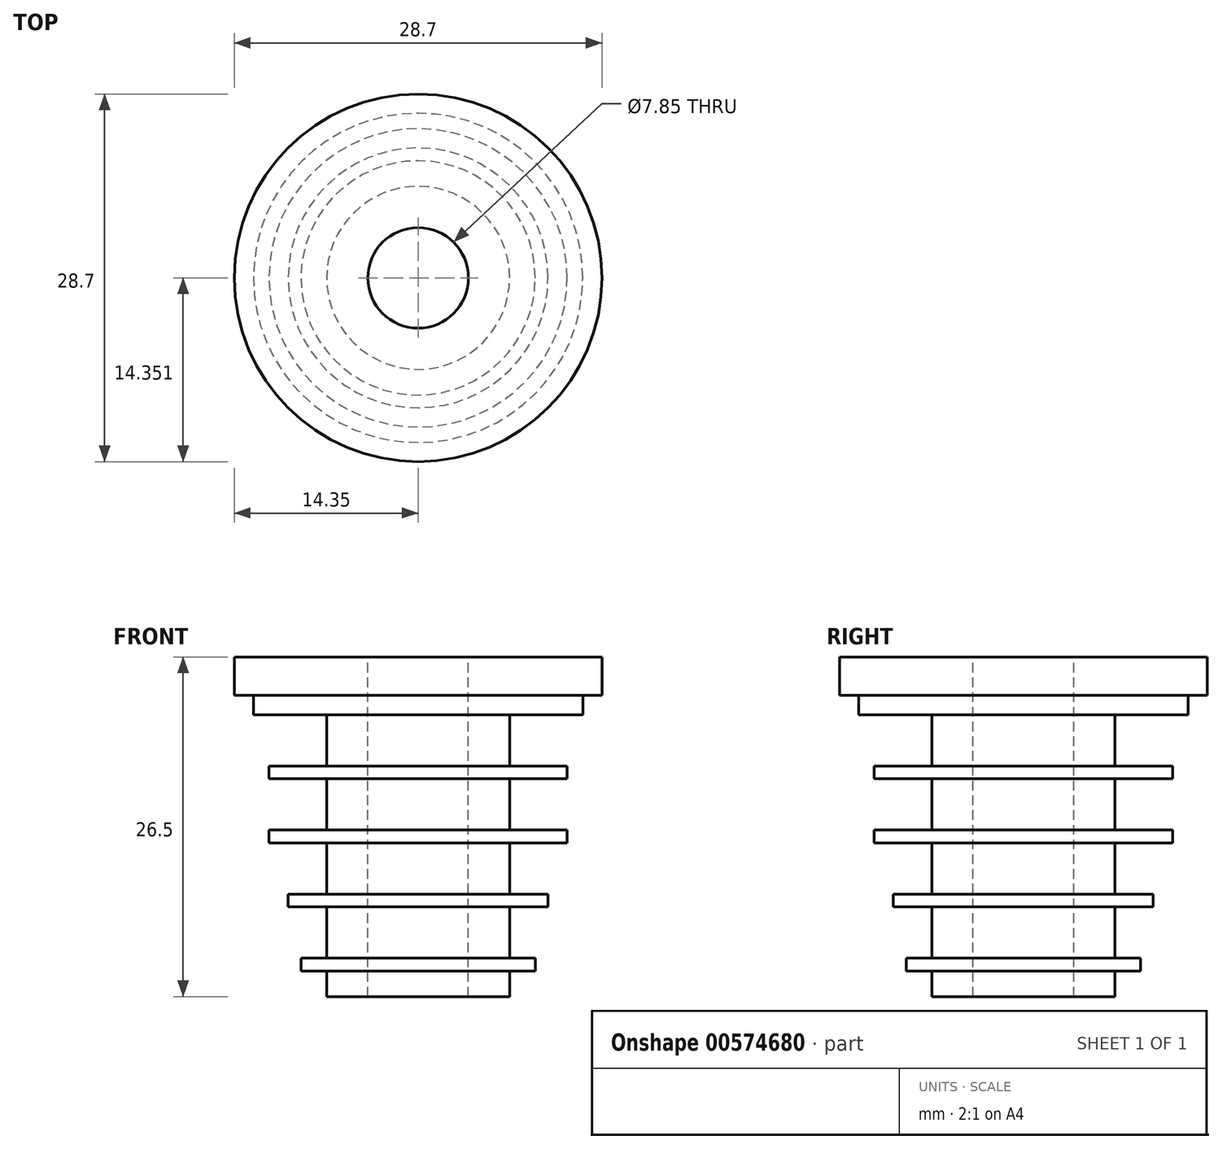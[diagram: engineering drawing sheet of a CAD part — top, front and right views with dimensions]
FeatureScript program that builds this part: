
annotation { "Feature Type Name" : "Feature", "Feature Type Description" : "" }
export const myFeature = defineFeature(function(context is Context, id is Id, definition is map)
    precondition{}
    {
        {
            var Q0;
            Q0=qCreatedBy(makeId("Right.planeOp"),FACE);
            var sketch = newSketch(context, id + "F0", { "sketchPlane" : qUnion([Q0])});
            skLineSegment(sketch, "E0", {"start": v(-3.9, -22.98) * mm, "end": v(-3.9, -0.04) * mm});
            skLineSegment(sketch, "E1", {"start": v(-3.9, -0.04) * mm, "end": v(-14.32, -0.04) * mm});
            skLineSegment(sketch, "E2", {"start": v(-14.32, -0.04) * mm, "end": v(-14.32, -3.04) * mm});
            skLineSegment(sketch, "E3", {"start": v(-14.32, -3.04) * mm, "end": v(-12.82, -3.04) * mm});
            skLineSegment(sketch, "E4", {"start": v(-12.82, -3.04) * mm, "end": v(-12.82, -4.54) * mm});
            skLineSegment(sketch, "E5", {"start": v(-12.82, -4.54) * mm, "end": v(-7.11, -4.54) * mm});
            skLineSegment(sketch, "E6", {"start": v(-7.11, -4.54) * mm, "end": v(-7.11, -8.54) * mm});
            skLineSegment(sketch, "E7", {"start": v(-7.11, -8.54) * mm, "end": v(-11.61, -8.54) * mm});
            skLineSegment(sketch, "E8", {"start": v(-11.61, -8.54) * mm, "end": v(-11.61, -9.54) * mm});
            skLineSegment(sketch, "E9", {"start": v(-11.61, -9.54) * mm, "end": v(-7.11, -9.54) * mm});
            skLineSegment(sketch, "E10", {"start": v(-7.11, -9.54) * mm, "end": v(-7.11, -13.54) * mm});
            skLineSegment(sketch, "E11", {"start": v(-7.11, -13.54) * mm, "end": v(-11.61, -13.54) * mm});
            skLineSegment(sketch, "E12", {"start": v(-11.61, -13.54) * mm, "end": v(-11.61, -14.54) * mm});
            skLineSegment(sketch, "E13", {"start": v(-11.61, -14.54) * mm, "end": v(-7.11, -14.54) * mm});
            skLineSegment(sketch, "E14", {"start": v(-7.11, -14.54) * mm, "end": v(-7.11, -18.54) * mm});
            skLineSegment(sketch, "E15", {"start": v(-7.11, -18.54) * mm, "end": v(-10.11, -18.54) * mm});
            skLineSegment(sketch, "E16", {"start": v(-10.11, -18.54) * mm, "end": v(-10.11, -19.54) * mm});
            skLineSegment(sketch, "E17", {"start": v(-10.11, -19.54) * mm, "end": v(-7.11, -19.54) * mm});
            skLineSegment(sketch, "E18", {"start": v(-7.11, -19.54) * mm, "end": v(-7.11, -23.54) * mm});
            skLineSegment(sketch, "E19", {"start": v(-7.11, -23.54) * mm, "end": v(-9.11, -23.54) * mm});
            skLineSegment(sketch, "E20", {"start": v(-9.11, -23.54) * mm, "end": v(-9.11, -24.54) * mm});
            skLineSegment(sketch, "E21", {"start": v(-9.11, -24.54) * mm, "end": v(-7.11, -24.54) * mm});
            skLineSegment(sketch, "E22", {"start": v(-7.11, -24.54) * mm, "end": v(-7.11, -26.54) * mm});
            skLineSegment(sketch, "E23", {"start": v(-7.11, -26.54) * mm, "end": v(-3.9, -26.54) * mm});
            skLineSegment(sketch, "E24", {"start": v(-3.9, -26.54) * mm, "end": v(-3.9, -22.98) * mm});
            skLineSegment(sketch, "E25", {"start": v(0.03, -0.04) * mm, "end": v(0.03, -26.58) * mm});
            skSolve(sketch);
        }
        {
            var Q0;
            Q0=makeQuery(id+"F0.imprint","IMPRINT",FACE,{"disambiguationData":[TD([[makeQuery(id+"F0.imprint","IMPRINT",EDGE,{"derivedFrom":sQuery(id+"F0.wireOp",EDGE,"E0")}),1.0]])]});
            var Q1;
            Q1=sQuery(id+"F0.wireOp",EDGE,"E25");
            revolve(context, id + "F1", {"entities" : qUnion([Q0]), "axis" : qUnion([Q1]), "revolveType" : RevolveType.FULL});
        }
    });
